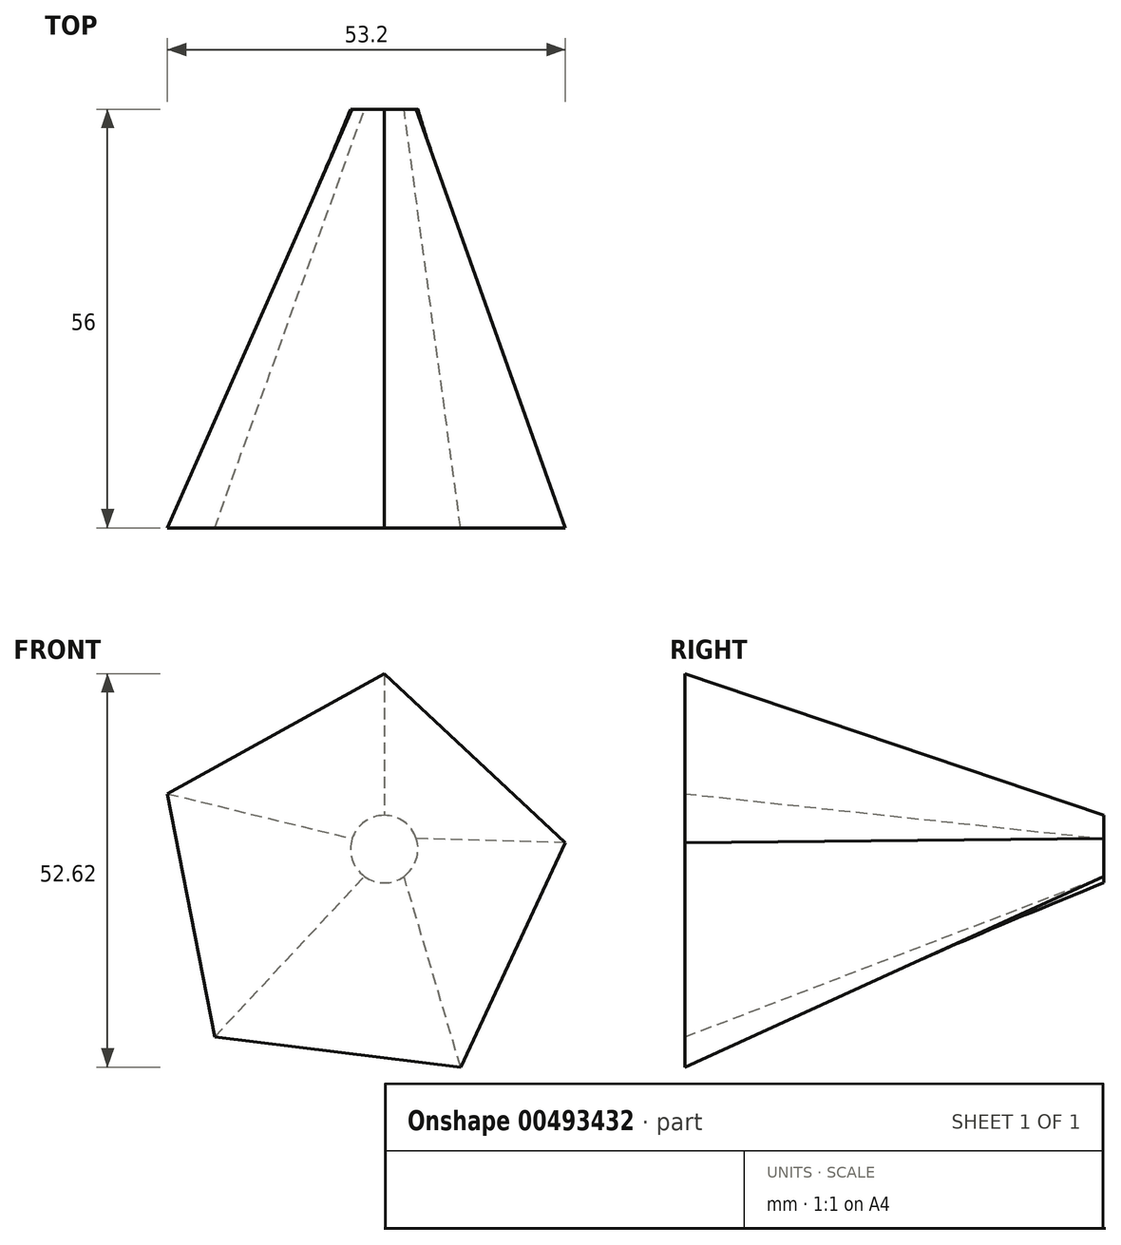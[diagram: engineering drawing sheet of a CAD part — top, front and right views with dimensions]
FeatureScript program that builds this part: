
annotation { "Feature Type Name" : "Feature", "Feature Type Description" : "" }
export const myFeature = defineFeature(function(context is Context, id is Id, definition is map)
    precondition{}
    {
        {
            var Q0;
            Q0=qCreatedBy(makeId("Front.planeOp"),FACE);
            var sketch = newSketch(context, id + "F0", { "sketchPlane" : qUnion([Q0])});
            skCircle(sketch, "E0.cCircle", {"center": v(-3.44, 0) * mm, "radius": 28.18 * mm, "construction": true});
            skLineSegment(sketch, "E0.0", {"start": v(0, 27.97) * mm, "end": v(24.22, 5.37) * mm});
            skLineSegment(sketch, "E0.1", {"start": v(24.22, 5.37) * mm, "end": v(10.21, -24.65) * mm});
            skLineSegment(sketch, "E0.2", {"start": v(10.21, -24.65) * mm, "end": v(-22.67, -20.6) * mm});
            skLineSegment(sketch, "E0.3", {"start": v(-22.67, -20.6) * mm, "end": v(-28.98, 11.92) * mm});
            skLineSegment(sketch, "E0.4", {"start": v(-28.98, 11.92) * mm, "end": v(0, 27.97) * mm});
            skSolve(sketch);
        }
        {
            var Q0;
            Q0=qCreatedBy(makeId("Front.planeOp"),FACE);
            cPlane(context, id + "F1", {"entities" : qUnion([Q0]), "cplaneType" : CPlaneType.OFFSET, "offset" : 56 * mm, "oppositeDirection" : true, "width" : 150 * mm, "height" : 150 * mm});
        }
        {
            var Q0;
            Q0=qCreatedBy(id+"F1.planeOp",FACE);
            var sketch = newSketch(context, id + "F2", { "sketchPlane" : qUnion([Q0])});
            skCircle(sketch, "E1", {"center": v(0, 4.51) * mm, "radius": 4.51 * mm});
            skSolve(sketch);
        }
        {
            var Q0;
            Q0=makeQuery(id+"F0.imprint","IMPRINT",FACE,{"disambiguationData":[TD([[makeQuery(id+"F0.imprint","IMPRINT",EDGE,{"derivedFrom":sQuery(id+"F0.wireOp",EDGE,"E0.0")}),-1.0]])]});
            var Q1;
            Q1=makeQuery(id+"F2.imprint","IMPRINT",FACE,{"disambiguationData":[TD([[makeQuery(id+"F2.imprint","IMPRINT",EDGE,{"derivedFrom":sQuery(id+"F2.wireOp",EDGE,"E1")}),1.0]])]});
            loft(context, id + "F3", {"sheetProfilesArray" : [{ "sheetProfileEntities" : qUnion([Q0]) }, { "sheetProfileEntities" : qUnion([Q1]) }]});
        }
    });
